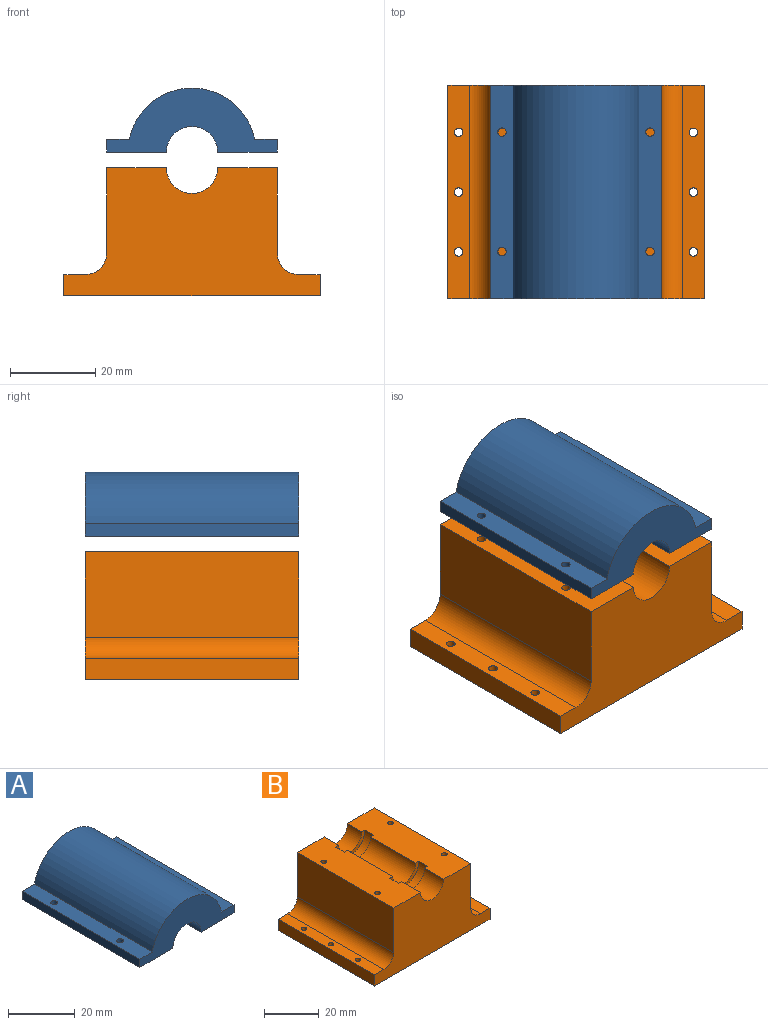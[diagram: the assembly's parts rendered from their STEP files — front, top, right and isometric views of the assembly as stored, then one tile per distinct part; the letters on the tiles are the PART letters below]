
ASSEMBLY  parts=2 mates=1
PART A: 22 faces, bbox 40x50x15 mm
  f0: plane 50x14mm, normal (0,0,-1), area 679.3mm2, adj f1,f2,f3,f9,f10,f11,f12,f13
  f1: cylinder r=6mm len=23.5mm, axis (0,-1,0), area 443mm2, adj f0,f8,f13,f17
  f2: cylinder r=6mm len=12mm, axis (0,-1,0), area 188.5mm2, adj f0,f8,f11,f14
  f3: plane 50x3mm, normal (1,0,0), area 150mm2, adj f0,f4,f10,f11
  f4: plane 50x5.3mm, normal (0,0,1), area 258.9mm2, adj f3,f5,f10,f11,f20,f21
  f5: cylinder r=15mm len=50mm, axis (0,-1,0), area 2054.2mm2, adj f4,f6,f10,f11
  f6: plane 50x5.3mm, normal (0,0,1), area 258.9mm2, adj f5,f7,f10,f11,f18,f19
  f7: plane 50x3mm, normal (-1,0,0), area 150mm2, adj f6,f8,f10,f11
  f8: plane 50x14mm, normal (0,0,-1), area 679.3mm2, adj f1,f2,f7,f9,f10,f11,f12,f13
  f9: cylinder r=6mm len=12mm, axis (0,-1,0), area 141.4mm2, adj f0,f8,f10,f16
  f10: plane 40x15mm, normal (0,1,0), area 327.5mm2, adj f0,f3,f4,f5,f6,f7,f8,f9
  f11: plane 40x15mm, normal (0,-1,0), area 327.5mm2, adj f0,f2,f3,f4,f5,f6,f7,f8
  f12: cylinder r=7.6mm len=15.2mm, axis (0,-1,0), area 107.4mm2, adj f0,f8,f13,f14
  f13: plane 15.2x7.6mm, normal (0,-1,0), area 34.2mm2, adj f0,f1,f8,f12
  f14: plane 15.2x7.6mm, normal (0,1,0), area 34.2mm2, adj f0,f2,f8,f12
  f15: cylinder r=7.6mm len=15.2mm, axis (0,-1,0), area 107.4mm2, adj f0,f8,f16,f17
  f16: plane 15.2x7.6mm, normal (0,-1,0), area 34.2mm2, adj f0,f8,f9,f15
  f17: plane 15.2x7.6mm, normal (0,1,0), area 34.2mm2, adj f0,f1,f8,f15
  f18: cylinder r=1mm len=3mm, axis (0,0,1), area 18.8mm2, adj f6,f8
  f19: cylinder r=1mm len=3mm, axis (0,0,1), area 18.8mm2, adj f6,f8
  f20: cylinder r=1mm len=3mm, axis (0,0,1), area 18.8mm2, adj f0,f4
  f21: cylinder r=1mm len=3mm, axis (0,0,1), area 18.8mm2, adj f0,f4
PART B: 36 faces, bbox 60x50x30 mm
  f0: plane 50x14mm, normal (0,0,1), area 679.3mm2, adj f3,f4,f5,f6,f9,f12,f16,f17
  f1: plane 50x14mm, normal (0,0,1), area 679.3mm2, adj f3,f4,f5,f6,f9,f14,f16,f17
  f2: plane 60x50mm, normal (0,0,-1), area 2981.2mm2, adj f5,f6,f7,f8,f22,f23,f24,f25
  f3: cylinder r=6mm len=12mm, axis (0,-1,0), area 141.4mm2, adj f0,f1,f5,f20
  f4: cylinder r=6mm len=23.5mm, axis (0,-1,0), area 443mm2, adj f0,f1,f17,f21
  f5: plane 60x30mm, normal (0,1,0), area 1254.2mm2, adj f0,f1,f2,f3,f7,f8,f10,f11
  f6: plane 60x30mm, normal (0,-1,0), area 1254.2mm2, adj f0,f1,f2,f7,f8,f9,f10,f11
  f7: plane 50x5mm, normal (-1,0,0), area 250mm2, adj f2,f5,f6,f10
  f8: plane 50x5mm, normal (1,0,0), area 250mm2, adj f2,f5,f6,f13
  f9: cylinder r=6mm len=12mm, axis (0,-1,0), area 188.5mm2, adj f0,f1,f6,f18
  f10: plane 50x5mm, normal (0,0,1), area 240.6mm2, adj f5,f6,f7,f11,f22,f26,f27
  f11: cylinder r=5mm len=50mm, axis (0,-1,0), area 392.7mm2, adj f5,f6,f10,f12
  f12: plane 50x20mm, normal (-1,0,0), area 1000mm2, adj f0,f5,f6,f11
  f13: plane 50x5mm, normal (0,0,1), area 240.6mm2, adj f5,f6,f8,f15,f23,f24,f25
  f14: plane 50x20mm, normal (1,0,0), area 1000mm2, adj f1,f5,f6,f15
  f15: cylinder r=5mm len=50mm, axis (0,-1,0), area 392.7mm2, adj f5,f6,f13,f14
  f16: cylinder r=7.6mm len=15.2mm, axis (0,-1,0), area 107.4mm2, adj f0,f1,f17,f18
  f17: plane 15.2x7.6mm, normal (0,-1,0), area 34.2mm2, adj f0,f1,f4,f16
  f18: plane 15.2x7.6mm, normal (0,1,0), area 34.2mm2, adj f0,f1,f9,f16
  f19: cylinder r=7.6mm len=15.2mm, axis (0,-1,0), area 107.4mm2, adj f0,f1,f20,f21
  f20: plane 15.2x7.6mm, normal (0,-1,0), area 34.2mm2, adj f0,f1,f3,f19
  f21: plane 15.2x7.6mm, normal (0,1,0), area 34.2mm2, adj f0,f1,f4,f19
  f22: cylinder r=1mm len=5mm, axis (0,0,1), area 31.4mm2, adj f2,f10
  f23: cylinder r=1mm len=5mm, axis (0,0,1), area 31.4mm2, adj f2,f13
  f24: cylinder r=1mm len=5mm, axis (0,0,1), area 31.4mm2, adj f2,f13
  f25: cylinder r=1mm len=5mm, axis (0,0,1), area 31.4mm2, adj f2,f13
  f26: cylinder r=1mm len=5mm, axis (0,0,1), area 31.4mm2, adj f2,f10
  f27: cylinder r=1mm len=5mm, axis (0,0,1), area 31.4mm2, adj f2,f10
  f28: cylinder r=1mm len=5mm, axis (0,0,1), area 31.4mm2, adj f1,f29
  f29: plane 2x2mm, normal (0,0,1), area 3.1mm2, adj f28
  f30: cylinder r=1mm len=5mm, axis (0,0,1), area 31.4mm2, adj f1,f31
  f31: plane 2x2mm, normal (0,0,1), area 3.1mm2, adj f30
  f32: cylinder r=1mm len=5mm, axis (0,0,1), area 31.4mm2, adj f0,f33
  f33: plane 2x2mm, normal (0,0,1), area 3.1mm2, adj f32
  f34: cylinder r=1mm len=5mm, axis (0,0,1), area 31.4mm2, adj f0,f35
  f35: plane 2x2mm, normal (0,0,1), area 3.1mm2, adj f34
PLACE A t=(-23.63,-24.85,52.07)mm
PLACE B t=(4.76,-29.32,18.37)mm
MATE planar A.f3 <-> B.f14  axis (1,0,0) through (16.37,0.15,53.57)mm
